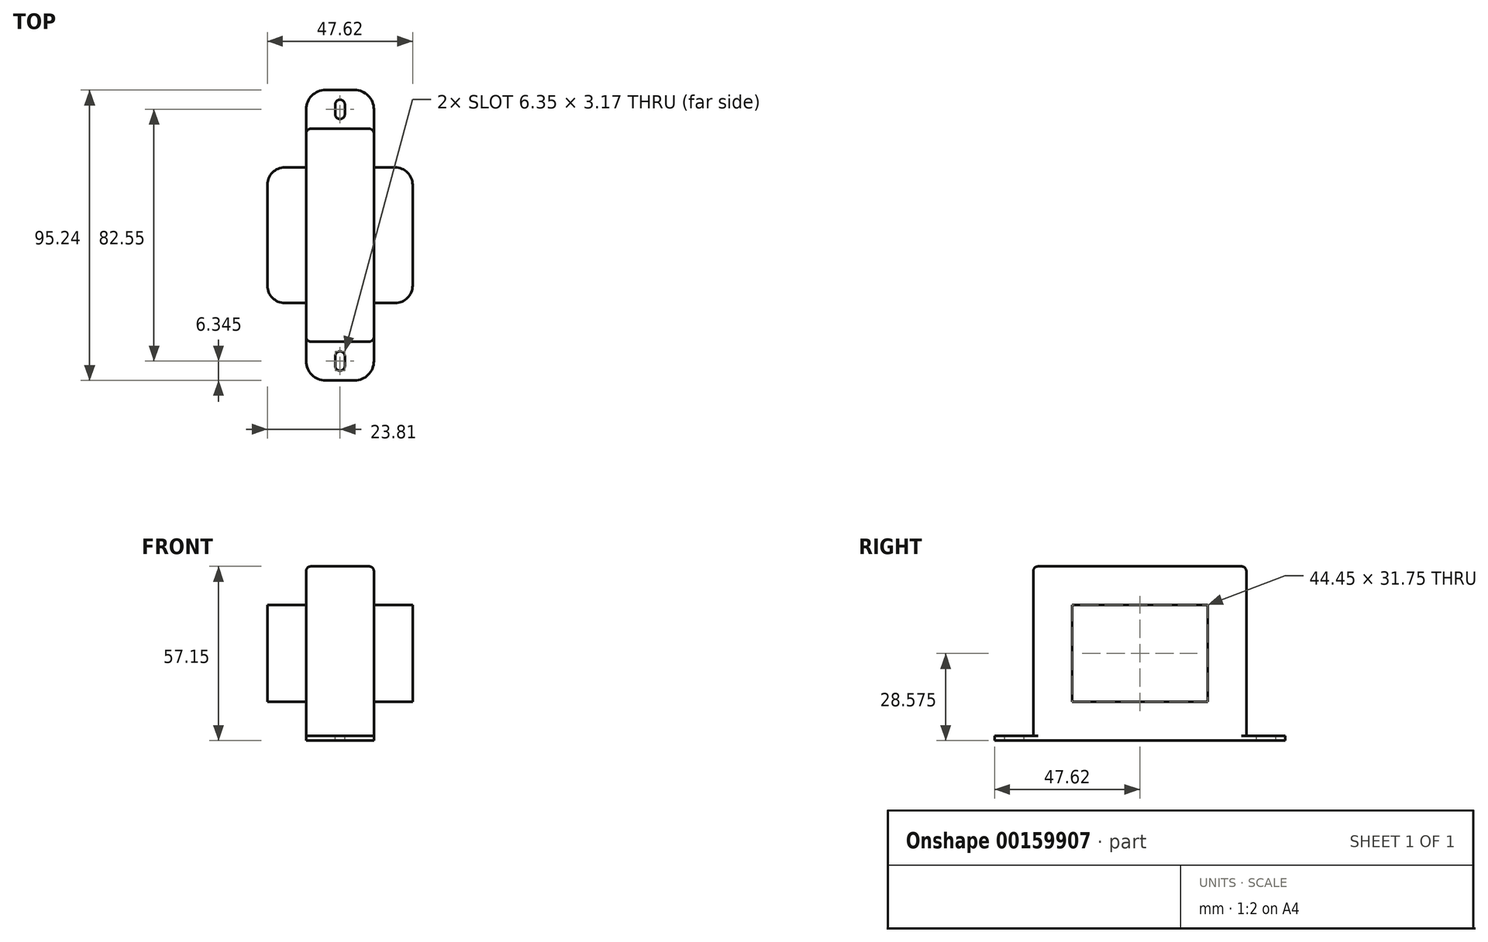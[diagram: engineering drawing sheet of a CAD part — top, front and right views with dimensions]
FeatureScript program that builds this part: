
annotation { "Feature Type Name" : "Feature", "Feature Type Description" : "" }
export const myFeature = defineFeature(function(context is Context, id is Id, definition is map)
    precondition{}
    {
        {
            var Q0;
            Q0=qCreatedBy(makeId("Top.planeOp"),FACE);
            var sketch = newSketch(context, id + "F0", { "sketchPlane" : qUnion([Q0])});
            skLineSegment(sketch, "E0.bottom", {"start": v(11.11, -34.93) * mm, "end": v(-11.11, -34.93) * mm});
            skLineSegment(sketch, "E0.top", {"start": v(11.11, 34.93) * mm, "end": v(-11.11, 34.93) * mm});
            skLineSegment(sketch, "E0.left", {"start": v(11.11, -34.93) * mm, "end": v(11.11, 34.92) * mm});
            skLineSegment(sketch, "E0.right", {"start": v(-11.11, -34.93) * mm, "end": v(-11.11, 34.92) * mm});
            skPoint(sketch, "E0.middle", {"position": v(0, 0) * mm});
            skSolve(sketch);
        }
        {
            var Q0;
            Q0=makeQuery(id+"F0.imprint","IMPRINT",FACE,{"disambiguationData":[TD([[makeQuery(id+"F0.imprint","IMPRINT",EDGE,{"derivedFrom":sQuery(id+"F0.wireOp",EDGE,"E0.bottom")}),-1.0]])]});
            extrude(context, id + "F1", {"entities" : qUnion([Q0]), "depth" : 57.15 * mm});
        }
        {
            var Q0;
            Q0=makeQuery(id+"F1.opExtrude","CAP_FACE",FACE,{"disambiguationData":[OSD([sQuery(id+"F0.wireOp",EDGE,"E0.bottom"),sQuery(id+"F0.wireOp",EDGE,"E0.top"),sQuery(id+"F0.wireOp",EDGE,"E0.left"),sQuery(id+"F0.wireOp",EDGE,"E0.right")])],"isStart":true});
            var sketch = newSketch(context, id + "F2", { "sketchPlane" : qUnion([Q0])});
            skLineSegment(sketch, "E1.bottom", {"start": v(-11.11, 34.93) * mm, "end": v(11.11, 34.93) * mm});
            skLineSegment(sketch, "E1.top", {"start": v(-11.11, 47.63) * mm, "end": v(11.11, 47.63) * mm});
            skLineSegment(sketch, "E1.left", {"start": v(-11.11, 34.93) * mm, "end": v(-11.11, 47.63) * mm});
            skLineSegment(sketch, "E1.right", {"start": v(11.11, 34.93) * mm, "end": v(11.11, 47.63) * mm});
            skLineSegment(sketch, "E2", {"start": v(-11.11, 0) * mm, "end": v(11.11, 0) * mm, "construction": true});
            skLineSegment(sketch, "E3.MirrorCS", {"start": v(11.11, -34.93) * mm, "end": v(11.11, -47.63) * mm});
            skLineSegment(sketch, "E4.MirrorCS", {"start": v(-11.11, -34.92) * mm, "end": v(-11.11, -47.62) * mm});
            skLineSegment(sketch, "E5.MirrorCS", {"start": v(-11.11, -47.62) * mm, "end": v(11.11, -47.63) * mm});
            skLineSegment(sketch, "E6.MirrorCS", {"start": v(-11.11, -34.92) * mm, "end": v(11.11, -34.93) * mm});
            skSolve(sketch);
        }
        {
            var Q0;
            Q0=makeQuery(id+"F2.imprint","IMPRINT",FACE,{"disambiguationData":[TD([[makeQuery(id+"F2.imprint","IMPRINT",EDGE,{"derivedFrom":sQuery(id+"F2.wireOp",EDGE,"E1.bottom")}),-1.0]])]});
            var Q1;
            Q1=makeQuery(id+"F2.imprint","IMPRINT",FACE,{"disambiguationData":[TD([[makeQuery(id+"F2.imprint","IMPRINT",EDGE,{"derivedFrom":sQuery(id+"F2.wireOp",EDGE,"E3.MirrorCS")}),-1.0]])]});
            extrude(context, id + "F3", {"entities" : qUnion([Q0, Q1]), "operationType" : NewBodyOperationType.ADD, "oppositeDirection" : true, "depth" : 1.59 * mm});
        }
        {
            var Q0;
            Q0=makeQuery(id+"F3.opExtrude","SWEPT_EDGE",EDGE,{"disambiguationData":[OSD([sQuery(id+"F2.wireOp",EDGE,"E1.top"),sQuery(id+"F2.wireOp",EDGE,"E1.left")])]});
            var Q1;
            Q1=makeQuery(id+"F3.opExtrude","SWEPT_EDGE",EDGE,{"disambiguationData":[OSD([sQuery(id+"F2.wireOp",EDGE,"E1.top"),sQuery(id+"F2.wireOp",EDGE,"E1.right")])]});
            var Q2;
            Q2=makeQuery(id+"F3.opExtrude","SWEPT_EDGE",EDGE,{"disambiguationData":[OSD([sQuery(id+"F2.wireOp",EDGE,"E4.MirrorCS"),sQuery(id+"F2.wireOp",EDGE,"E5.MirrorCS")])]});
            var Q3;
            Q3=makeQuery(id+"F3.opExtrude","SWEPT_EDGE",EDGE,{"disambiguationData":[OSD([sQuery(id+"F2.wireOp",EDGE,"E3.MirrorCS"),sQuery(id+"F2.wireOp",EDGE,"E5.MirrorCS")])]});
            fillet(context, id + "F4", {"entities" : qUnion([Q0, Q1, Q2, Q3]), "radius" : 6.35 * mm, "tangentPropagation" : true, "allowEdgeOverflow" : false});
        }
        {
            var Q0;
            Q0=makeQuery(id+"F3.opExtrude","CAP_FACE",FACE,{"disambiguationData":[OSD([sQuery(id+"F2.wireOp",EDGE,"E3.MirrorCS"),sQuery(id+"F2.wireOp",EDGE,"E4.MirrorCS"),sQuery(id+"F2.wireOp",EDGE,"E5.MirrorCS"),sQuery(id+"F2.wireOp",EDGE,"E6.MirrorCS")])],"isStart":false});
            var sketch = newSketch(context, id + "F5", { "sketchPlane" : qUnion([Q0])});
            skLineSegment(sketch, "E7", {"start": v(0, 47.63) * mm, "end": v(0, 34.93) * mm, "construction": true});
            skLineSegment(sketch, "E8", {"start": v(-12.7, 0) * mm, "end": v(12.7, 0) * mm, "construction": true});
            skLineSegment(sketch, "E9.MirrorCS", {"start": v(0, -47.63) * mm, "end": v(0, -34.93) * mm, "construction": true});
            skPoint(sketch, "E10", {"position": v(0, 41.28) * mm});
            skPoint(sketch, "E11", {"position": v(0, -41.28) * mm});
            skLineSegment(sketch, "E12.bottom", {"start": v(1.59, 38.1) * mm, "end": v(-1.59, 38.1) * mm});
            skLineSegment(sketch, "E12.top", {"start": v(1.59, 44.45) * mm, "end": v(-1.59, 44.45) * mm});
            skLineSegment(sketch, "E12.left", {"start": v(1.59, 38.1) * mm, "end": v(1.59, 44.45) * mm});
            skLineSegment(sketch, "E12.right", {"start": v(-1.59, 38.1) * mm, "end": v(-1.59, 44.45) * mm});
            skLineSegment(sketch, "E13.bottom", {"start": v(1.59, -44.45) * mm, "end": v(-1.59, -44.45) * mm});
            skLineSegment(sketch, "E13.top", {"start": v(1.59, -38.1) * mm, "end": v(-1.59, -38.1) * mm});
            skLineSegment(sketch, "E13.left", {"start": v(1.59, -44.45) * mm, "end": v(1.59, -38.1) * mm});
            skLineSegment(sketch, "E13.right", {"start": v(-1.59, -44.45) * mm, "end": v(-1.59, -38.1) * mm});
            skSolve(sketch);
        }
        {
            var Q0;
            Q0=makeQuery(id+"F5.imprint","IMPRINT",FACE,{"disambiguationData":[TD([[makeQuery(id+"F5.imprint","IMPRINT",EDGE,{"derivedFrom":sQuery(id+"F5.wireOp",EDGE,"E12.bottom")}),-1.0]])]});
            var Q1;
            Q1=makeQuery(id+"F5.imprint","IMPRINT",FACE,{"disambiguationData":[TD([[makeQuery(id+"F5.imprint","IMPRINT",EDGE,{"derivedFrom":sQuery(id+"F5.wireOp",EDGE,"E13.bottom")}),-1.0]])]});
            extrude(context, id + "F6", {"entities" : qUnion([Q0, Q1]), "operationType" : NewBodyOperationType.REMOVE, "oppositeDirection" : true, "depth" : 25.4 * mm});
        }
        {
            var Q0;
            Q0=makeQuery(id+"F6.boolean.opBoolean","COPY",EDGE,{"derivedFrom":makeQuery(id+"F6.opExtrude","SWEPT_EDGE",EDGE,{"disambiguationData":[OSD([sQuery(id+"F5.wireOp",EDGE,"E12.top"),sQuery(id+"F5.wireOp",EDGE,"E12.left")])]})});
            var Q1;
            Q1=makeQuery(id+"F6.boolean.opBoolean","COPY",EDGE,{"derivedFrom":makeQuery(id+"F6.opExtrude","SWEPT_EDGE",EDGE,{"disambiguationData":[OSD([sQuery(id+"F5.wireOp",EDGE,"E12.top"),sQuery(id+"F5.wireOp",EDGE,"E12.right")])]})});
            var Q2;
            Q2=makeQuery(id+"F6.boolean.opBoolean","COPY",EDGE,{"derivedFrom":makeQuery(id+"F6.opExtrude","SWEPT_EDGE",EDGE,{"disambiguationData":[OSD([sQuery(id+"F5.wireOp",EDGE,"E12.bottom"),sQuery(id+"F5.wireOp",EDGE,"E12.right")])]})});
            var Q3;
            Q3=makeQuery(id+"F6.boolean.opBoolean","COPY",EDGE,{"derivedFrom":makeQuery(id+"F6.opExtrude","SWEPT_EDGE",EDGE,{"disambiguationData":[OSD([sQuery(id+"F5.wireOp",EDGE,"E12.bottom"),sQuery(id+"F5.wireOp",EDGE,"E12.left")])]})});
            var Q4;
            Q4=makeQuery(id+"F6.boolean.opBoolean","COPY",EDGE,{"derivedFrom":makeQuery(id+"F6.opExtrude","SWEPT_EDGE",EDGE,{"disambiguationData":[OSD([sQuery(id+"F5.wireOp",EDGE,"E13.top"),sQuery(id+"F5.wireOp",EDGE,"E13.left")])]})});
            var Q5;
            Q5=makeQuery(id+"F6.boolean.opBoolean","COPY",EDGE,{"derivedFrom":makeQuery(id+"F6.opExtrude","SWEPT_EDGE",EDGE,{"disambiguationData":[OSD([sQuery(id+"F5.wireOp",EDGE,"E13.top"),sQuery(id+"F5.wireOp",EDGE,"E13.right")])]})});
            var Q6;
            Q6=makeQuery(id+"F6.boolean.opBoolean","COPY",EDGE,{"derivedFrom":makeQuery(id+"F6.opExtrude","SWEPT_EDGE",EDGE,{"disambiguationData":[OSD([sQuery(id+"F5.wireOp",EDGE,"E13.bottom"),sQuery(id+"F5.wireOp",EDGE,"E13.right")])]})});
            var Q7;
            Q7=makeQuery(id+"F6.boolean.opBoolean","COPY",EDGE,{"derivedFrom":makeQuery(id+"F6.opExtrude","SWEPT_EDGE",EDGE,{"disambiguationData":[OSD([sQuery(id+"F5.wireOp",EDGE,"E13.bottom"),sQuery(id+"F5.wireOp",EDGE,"E13.left")])]})});
            fillet(context, id + "F7", {"entities" : qUnion([Q0, Q1, Q2, Q3, Q4, Q5, Q6, Q7]), "radius" : 1.59 * mm, "tangentPropagation" : true, "allowEdgeOverflow" : false});
        }
        {
            var Q0;
            Q0=makeQuery(id+"F3.boolean.opBoolean","MERGE",FACE,{"derivedFrom":[makeQuery(id+"F1.opExtrude","SWEPT_FACE",FACE,{"disambiguationData":[OSD([sQuery(id+"F0.wireOp",EDGE,"E0.left")])]}),makeQuery(id+"F3.opExtrude","SWEPT_FACE",FACE,{"disambiguationData":[OSD([sQuery(id+"F2.wireOp",EDGE,"E1.right")])]}),makeQuery(id+"F3.opExtrude","SWEPT_FACE",FACE,{"disambiguationData":[OSD([sQuery(id+"F2.wireOp",EDGE,"E3.MirrorCS")])]})]});
            var sketch = newSketch(context, id + "F8", { "sketchPlane" : qUnion([Q0])});
            skLineSegment(sketch, "E14", {"start": v(0, 0) * mm, "end": v(0, 57.15) * mm, "construction": true});
            skLineSegment(sketch, "E15.bottom", {"start": v(22.22, 12.7) * mm, "end": v(-22.23, 12.7) * mm});
            skLineSegment(sketch, "E15.top", {"start": v(22.22, 44.45) * mm, "end": v(-22.23, 44.45) * mm});
            skLineSegment(sketch, "E15.left", {"start": v(22.22, 12.7) * mm, "end": v(22.22, 44.45) * mm});
            skLineSegment(sketch, "E15.right", {"start": v(-22.23, 12.7) * mm, "end": v(-22.23, 44.45) * mm});
            skPoint(sketch, "E15.middle", {"position": v(0, 28.58) * mm});
            skSolve(sketch);
        }
        {
            var Q0;
            Q0=makeQuery(id+"F3.boolean.opBoolean","MERGE",FACE,{"derivedFrom":[makeQuery(id+"F1.opExtrude","SWEPT_FACE",FACE,{"disambiguationData":[OSD([sQuery(id+"F0.wireOp",EDGE,"E0.right")])]}),makeQuery(id+"F3.opExtrude","SWEPT_FACE",FACE,{"disambiguationData":[OSD([sQuery(id+"F2.wireOp",EDGE,"E1.left")])]}),makeQuery(id+"F3.opExtrude","SWEPT_FACE",FACE,{"disambiguationData":[OSD([sQuery(id+"F2.wireOp",EDGE,"E4.MirrorCS")])]})]});
            var sketch = newSketch(context, id + "F9", { "sketchPlane" : qUnion([Q0])});
            skLineSegment(sketch, "E16.bottom", {"start": v(22.23, 12.7) * mm, "end": v(-22.22, 12.7) * mm});
            skLineSegment(sketch, "E16.top", {"start": v(22.23, 44.45) * mm, "end": v(-22.22, 44.45) * mm});
            skLineSegment(sketch, "E16.left", {"start": v(22.23, 12.7) * mm, "end": v(22.23, 44.45) * mm});
            skLineSegment(sketch, "E16.right", {"start": v(-22.22, 12.7) * mm, "end": v(-22.22, 44.45) * mm});
            skPoint(sketch, "E16.middle", {"position": v(0, 28.58) * mm});
            skSolve(sketch);
        }
        {
            var Q0;
            Q0=makeQuery(id+"F8.imprint","IMPRINT",FACE,{"disambiguationData":[TD([[makeQuery(id+"F8.imprint","IMPRINT",EDGE,{"derivedFrom":sQuery(id+"F8.wireOp",EDGE,"E15.bottom")}),-1.0]])]});
            extrude(context, id + "F10", {"entities" : qUnion([Q0]), "operationType" : NewBodyOperationType.ADD, "depth" : 12.7 * mm});
        }
        {
            var Q0;
            Q0=makeQuery(id+"F9.imprint","IMPRINT",FACE,{"disambiguationData":[TD([[makeQuery(id+"F9.imprint","IMPRINT",EDGE,{"derivedFrom":sQuery(id+"F9.wireOp",EDGE,"E16.bottom")}),-1.0]])]});
            extrude(context, id + "F11", {"entities" : qUnion([Q0]), "operationType" : NewBodyOperationType.ADD, "depth" : 12.7 * mm});
        }
        {
            var Q0;
            Q0=makeQuery(id+"F10.opExtrude","CAP_EDGE",EDGE,{"disambiguationData":[OSD([sQuery(id+"F8.wireOp",EDGE,"E15.right")])],"isStart":false});
            var Q1;
            Q1=makeQuery(id+"F10.opExtrude","CAP_EDGE",EDGE,{"disambiguationData":[OSD([sQuery(id+"F8.wireOp",EDGE,"E15.left")])],"isStart":false});
            var Q2;
            Q2=makeQuery(id+"F11.opExtrude","CAP_EDGE",EDGE,{"disambiguationData":[OSD([sQuery(id+"F9.wireOp",EDGE,"E16.left")])],"isStart":false});
            var Q3;
            Q3=makeQuery(id+"F11.opExtrude","CAP_EDGE",EDGE,{"disambiguationData":[OSD([sQuery(id+"F9.wireOp",EDGE,"E16.right")])],"isStart":false});
            fillet(context, id + "F12", {"entities" : qUnion([Q0, Q1, Q2, Q3]), "radius" : 5.7 * mm, "tangentPropagation" : true, "allowEdgeOverflow" : false});
        }
        {
            var Q0;
            Q0=makeQuery(id+"F1.opExtrude","SWEPT_EDGE",EDGE,{"disambiguationData":[OSD([sQuery(id+"F0.wireOp",EDGE,"E0.bottom"),sQuery(id+"F0.wireOp",EDGE,"E0.left")])]});
            var Q1;
            Q1=makeQuery(id+"F1.opExtrude","CAP_EDGE",EDGE,{"disambiguationData":[OSD([sQuery(id+"F0.wireOp",EDGE,"E0.left")])],"isStart":false});
            var Q2;
            Q2=makeQuery(id+"F1.opExtrude","SWEPT_EDGE",EDGE,{"disambiguationData":[OSD([sQuery(id+"F0.wireOp",EDGE,"E0.top"),sQuery(id+"F0.wireOp",EDGE,"E0.left")])]});
            var Q3;
            Q3=makeQuery(id+"F1.opExtrude","CAP_EDGE",EDGE,{"disambiguationData":[OSD([sQuery(id+"F0.wireOp",EDGE,"E0.bottom")])],"isStart":false});
            var Q4;
            Q4=makeQuery(id+"F1.opExtrude","CAP_EDGE",EDGE,{"disambiguationData":[OSD([sQuery(id+"F0.wireOp",EDGE,"E0.top")])],"isStart":false});
            var Q5;
            Q5=makeQuery(id+"F1.opExtrude","SWEPT_EDGE",EDGE,{"disambiguationData":[OSD([sQuery(id+"F0.wireOp",EDGE,"E0.bottom"),sQuery(id+"F0.wireOp",EDGE,"E0.right")])]});
            var Q6;
            Q6=makeQuery(id+"F1.opExtrude","CAP_EDGE",EDGE,{"disambiguationData":[OSD([sQuery(id+"F0.wireOp",EDGE,"E0.right")])],"isStart":false});
            var Q7;
            Q7=makeQuery(id+"F1.opExtrude","SWEPT_EDGE",EDGE,{"disambiguationData":[OSD([sQuery(id+"F0.wireOp",EDGE,"E0.top"),sQuery(id+"F0.wireOp",EDGE,"E0.right")])]});
            fillet(context, id + "F13", {"entities" : qUnion([Q0, Q1, Q2, Q3, Q4, Q5, Q6, Q7]), "radius" : 1.59 * mm, "tangentPropagation" : true, "allowEdgeOverflow" : false});
        }
    });
